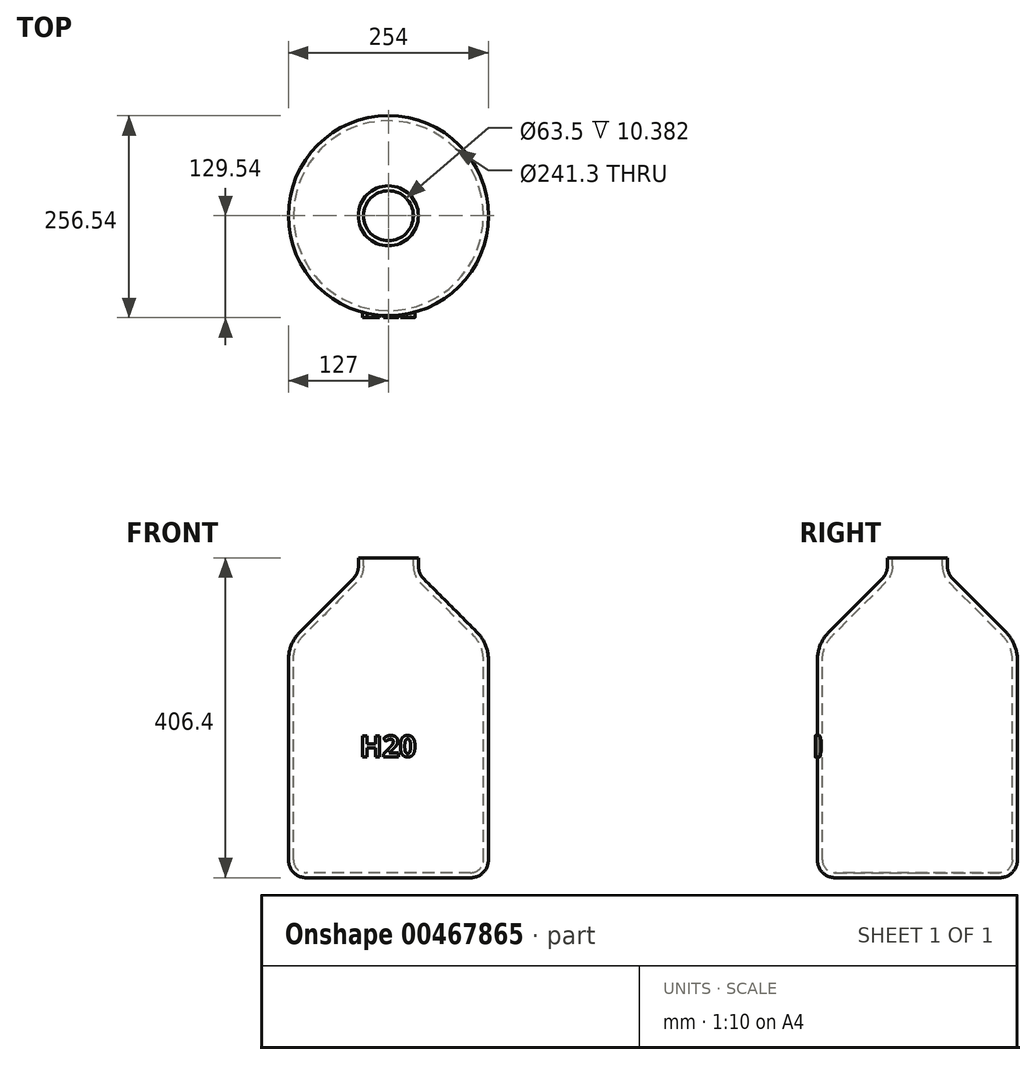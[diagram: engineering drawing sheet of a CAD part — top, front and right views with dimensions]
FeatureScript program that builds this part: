
annotation { "Feature Type Name" : "Feature", "Feature Type Description" : "" }
export const myFeature = defineFeature(function(context is Context, id is Id, definition is map)
    precondition{}
    {
        {
            var Q0;
            Q0=qCreatedBy(makeId("Front.planeOp"),FACE);
            var sketch = newSketch(context, id + "F0", { "sketchPlane" : qUnion([Q0])});
            skLineSegment(sketch, "E0", {"start": v(-38.1, 289.28) * mm, "end": v(-38.1, 278.9) * mm});
            skArc(sketch, "E1", {"start": v(-38.1, 278.9) * mm, "mid": v(-39.87, 269.99) * mm, "end": v(-44.92, 262.43) * mm});
            skLineSegment(sketch, "E2", {"start": v(-44.92, 262.43) * mm, "end": v(-112.22, 195.14) * mm});
            skArc(sketch, "E3", {"start": v(-112.22, 195.14) * mm, "mid": v(-123.16, 178.76) * mm, "end": v(-127, 159.45) * mm});
            skLineSegment(sketch, "E4", {"start": v(-127, 159.45) * mm, "end": v(-127, -94.55) * mm});
            skArc(sketch, "E5", {"start": v(-127, -94.55) * mm, "mid": v(-120.4, -110.5) * mm, "end": v(-104.44, -117.12) * mm});
            skLineSegment(sketch, "E6", {"start": v(-104.44, -117.12) * mm, "end": v(0, -117.12) * mm});
            skLineSegment(sketch, "E7", {"start": v(-38.1, 289.28) * mm, "end": v(0, 289.28) * mm});
            skLineSegment(sketch, "E8", {"start": v(0, 289.28) * mm, "end": v(0, -117.12) * mm});
            skSolve(sketch);
        }
        {
            var Q0;
            Q0=makeQuery(id+"F0.imprint","IMPRINT",FACE,{"disambiguationData":[TD([[makeQuery(id+"F0.imprint","IMPRINT",EDGE,{"derivedFrom":sQuery(id+"F0.wireOp",EDGE,"E0")}),1.0]])]});
            var Q1;
            Q1=sQuery(id+"F0.wireOp",EDGE,"E8");
            revolve(context, id + "F1", {"entities" : qUnion([Q0]), "axis" : qUnion([Q1]), "revolveType" : RevolveType.FULL});
        }
        {
            var Q0;
            Q0=makeQuery(id+"F1.opRevolve","SWEPT_FACE",FACE,{"disambiguationData":[OSD([sQuery(id+"F0.wireOp",EDGE,"E7")])]});
            shell(context, id + "F2", {"entities" : qUnion([Q0]), "thickness" : 6.35 * mm});
        }
        {
            var Q0;
            Q0=qCreatedBy(makeId("Front.planeOp"),FACE);
            cPlane(context, id + "F3", {"entities" : qUnion([Q0]), "cplaneType" : CPlaneType.OFFSET, "offset" : 129.54 * mm, "width" : 152.4 * mm, "height" : 152.4 * mm});
        }
        {
            var Q0;
            Q0=qCreatedBy(id+"F3.planeOp",FACE);
            var sketch = newSketch(context, id + "F4", { "sketchPlane" : qUnion([Q0])});
            skText(sketch, "E9", { "text": "H20", "fontName": "OpenSans-Bold.ttf"});
            const initialGuessF4  = {"E9": [-0.0362, 0.03655, 1, 0, 0.02692]};
            skSetInitialGuess(sketch, initialGuessF4);
            skSolve(sketch);
        }
        {
            var Q0;
            Q0 = qSketchRegion(id + "F4", true);
            var Q1;
            Q1=makeQuery(id+"F1.opRevolve","SWEPT_FACE",FACE,{"disambiguationData":[OSD([sQuery(id+"F0.wireOp",EDGE,"E4")])]});
            extrude(context, id + "F5", {"entities" : qUnion([Q0]), "operationType" : NewBodyOperationType.ADD, "endBound" : BoundingType.UP_TO_SURFACE, "oppositeDirection" : true, "endBoundEntityFace" : qUnion([Q1]), "depth" : 25.4 * mm});
        }
    });
